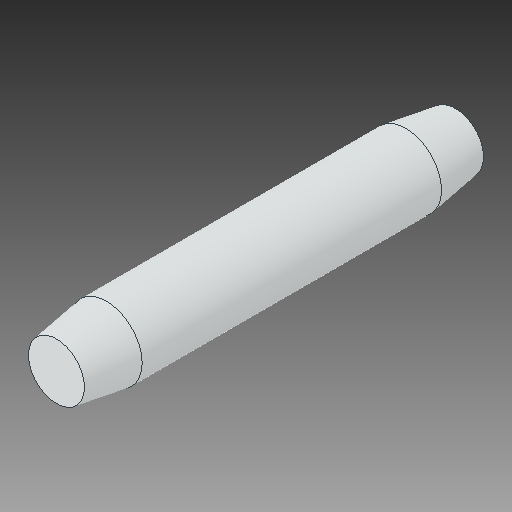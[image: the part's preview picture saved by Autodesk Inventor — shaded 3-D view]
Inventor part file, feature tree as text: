
AUTODESK INVENTOR PART (.ipt)
format: ipt  version: 2018 (Build 220112000, 112)  size: 93,696 bytes
history: native  units: in
note: dims shown in document units (in); Inventor stores cm internally (conversion verified against a paired STEP export)
features: chamfer x1
ambient origin geometry x8: Origin, YZ Plane, XZ Plane, XY Plane, X Axis, Y Axis, Z Axis, Center Point
bodies: Solid1 (feature_tree)
feature tree (1):
  chamfer  "Chamfer2"  [1 undecoded]
note: 1 required parameter value undecoded (feature->parameter linkage not recoverable at this tier; creation-order binding heuristic only, values carry confidence <= 0.55)
